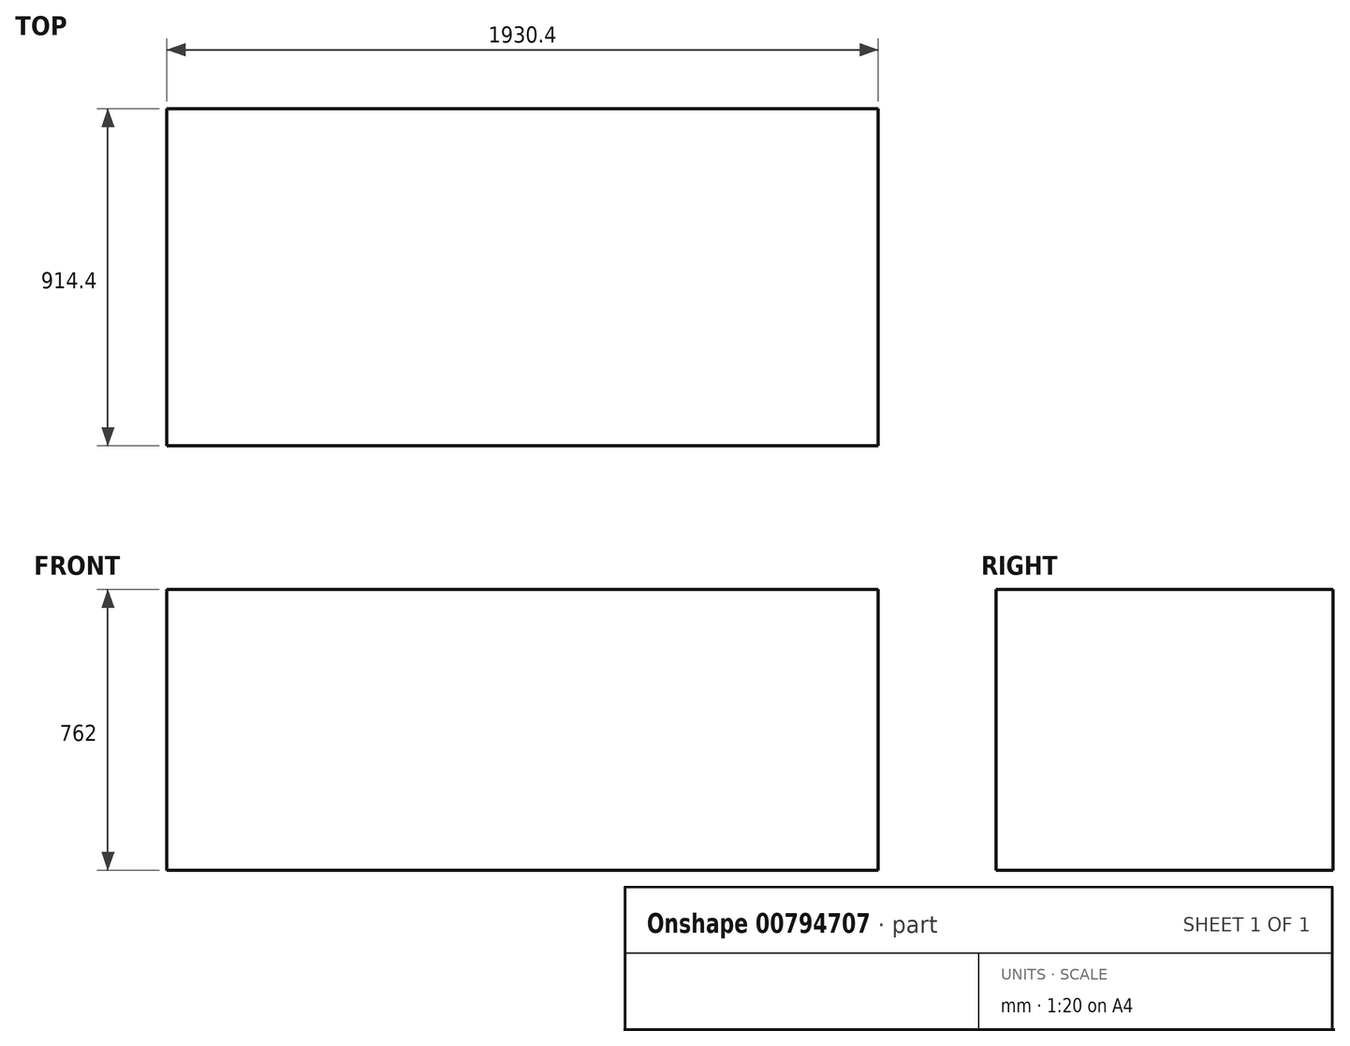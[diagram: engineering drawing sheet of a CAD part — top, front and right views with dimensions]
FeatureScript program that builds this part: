
annotation { "Feature Type Name" : "Feature", "Feature Type Description" : "" }
export const myFeature = defineFeature(function(context is Context, id is Id, definition is map)
    precondition{}
    {
        {
            var Q0;
            Q0=qCreatedBy(makeId("Top.planeOp"),FACE);
            var sketch = newSketch(context, id + "F0", { "sketchPlane" : qUnion([Q0])});
            skLineSegment(sketch, "E0.rect.bottom", {"start": v(965.2, 457.2) * mm, "end": v(-965.2, 457.2) * mm});
            skLineSegment(sketch, "E0.rect.top", {"start": v(965.2, -457.2) * mm, "end": v(-965.2, -457.2) * mm});
            skLineSegment(sketch, "E0.rect.left", {"start": v(965.2, 457.2) * mm, "end": v(965.2, -457.2) * mm});
            skLineSegment(sketch, "E0.rect.right", {"start": v(-965.2, 457.2) * mm, "end": v(-965.2, -457.2) * mm});
            skPoint(sketch, "E0.rect.middle", {"position": v(0, 0) * mm});
            skSolve(sketch);
        }
        {
            var Q0;
            Q0=makeQuery(id+"F0.imprint","IMPRINT",FACE,{"disambiguationData":[TD([[makeQuery(id+"F0.imprint","IMPRINT",EDGE,{"derivedFrom":sQuery(id+"F0.wireOp",EDGE,"E0.rect.bottom")}),1.0]])]});
            extrude(context, id + "F1", {"entities" : qUnion([Q0]), "depth" : 762 * mm});
        }
    });
